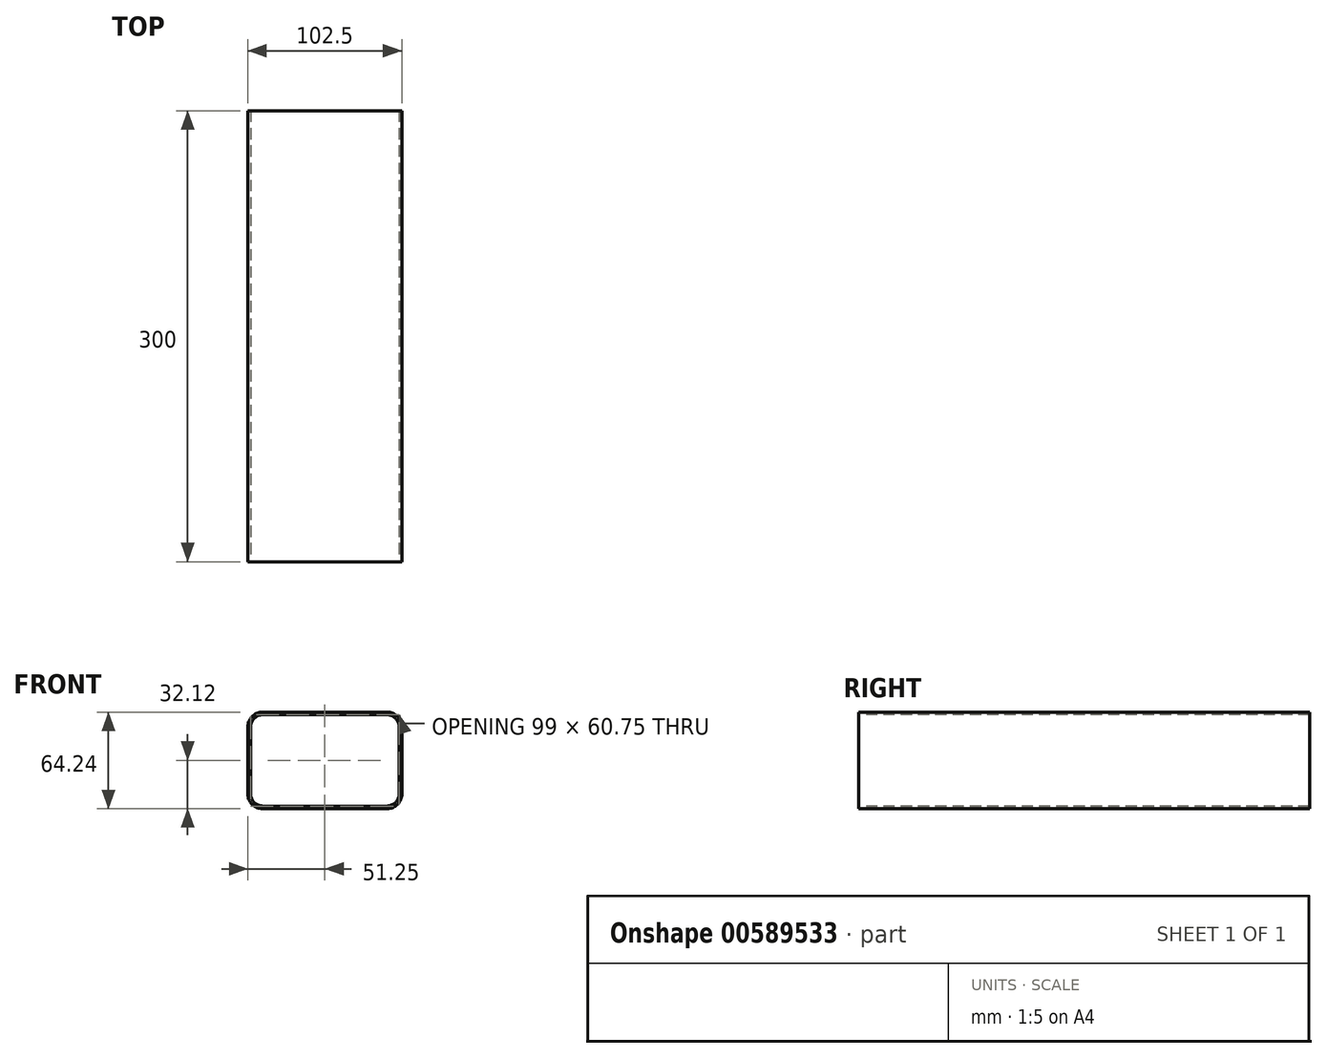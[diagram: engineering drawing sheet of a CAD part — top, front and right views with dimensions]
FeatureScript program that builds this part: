
annotation { "Feature Type Name" : "Feature", "Feature Type Description" : "" }
export const myFeature = defineFeature(function(context is Context, id is Id, definition is map)
    precondition{}
    {
        {
            var Q0;
            Q0=qCreatedBy(makeId("Front.planeOp"),FACE);
            var sketch = newSketch(context, id + "F0", { "sketchPlane" : qUnion([Q0]), "disableImprinting" : false});
            skLineSegment(sketch, "E0.bottom", {"start": v(41.25, 32.12) * mm, "end": v(-41.25, 32.12) * mm});
            skLineSegment(sketch, "E0.top", {"start": v(41.25, -32.13) * mm, "end": v(-41.25, -32.13) * mm});
            skLineSegment(sketch, "E0.left", {"start": v(51.25, 22.13) * mm, "end": v(51.25, -22.13) * mm});
            skLineSegment(sketch, "E0.right", {"start": v(-51.25, 22.12) * mm, "end": v(-51.25, -22.13) * mm});
            skPoint(sketch, "E0.middle", {"position": v(0, 0) * mm});
            skPoint(sketch, "E1.visualSharp", {"position": v(-51.25, 32.12) * mm});
            skArc(sketch, "E1.filletArc", {"start": v(-41.25, 32.12) * mm, "mid": v(-48.32, 29.2) * mm, "end": v(-51.25, 22.12) * mm});
            skPoint(sketch, "E2.visualSharp", {"position": v(51.25, 32.12) * mm});
            skArc(sketch, "E2.filletArc", {"start": v(51.25, 22.13) * mm, "mid": v(48.32, 29.2) * mm, "end": v(41.25, 32.13) * mm});
            skPoint(sketch, "E3.visualSharp", {"position": v(51.25, -32.13) * mm});
            skArc(sketch, "E3.filletArc", {"start": v(41.25, -32.13) * mm, "mid": v(48.32, -29.2) * mm, "end": v(51.25, -22.13) * mm});
            skPoint(sketch, "E4.visualSharp", {"position": v(-51.25, -32.13) * mm});
            skArc(sketch, "E4.filletArc", {"start": v(-51.25, -22.13) * mm, "mid": v(-48.32, -29.2) * mm, "end": v(-41.25, -32.13) * mm});
            skLineSegment(sketch, "E5.0", {"start": v(-49.5, 22.13) * mm, "end": v(-49.5, -22.13) * mm});
            skArc(sketch, "E5.1", {"start": v(-41.25, 30.38) * mm, "mid": v(-47.08, 27.96) * mm, "end": v(-49.5, 22.13) * mm});
            skArc(sketch, "E5.2", {"start": v(-49.5, -22.13) * mm, "mid": v(-47.08, -27.96) * mm, "end": v(-41.25, -30.38) * mm});
            skLineSegment(sketch, "E5.3", {"start": v(41.25, 30.38) * mm, "end": v(-41.25, 30.38) * mm});
            skLineSegment(sketch, "E5.4", {"start": v(41.25, -30.38) * mm, "end": v(-41.25, -30.38) * mm});
            skArc(sketch, "E5.5", {"start": v(41.25, -30.38) * mm, "mid": v(47.08, -27.96) * mm, "end": v(49.5, -22.13) * mm});
            skLineSegment(sketch, "E5.6", {"start": v(49.5, 22.13) * mm, "end": v(49.5, -22.13) * mm});
            skArc(sketch, "E5.7", {"start": v(49.5, 22.13) * mm, "mid": v(47.08, 27.96) * mm, "end": v(41.25, 30.38) * mm});
            skSolve(sketch);
        }
        {
            var Q0;
            Q0 = qSketchRegion(id + "F0", true);
            extrude(context, id + "F1", {"entities" : qUnion([Q0]), "flatOperationType" : FlatOperationType.REMOVE, "oppositeDirection" : true, "depth" : 300 * mm, "offsetDistance" : 25 * mm, "startOffsetBound" : StartOffsetType.BLIND, "startOffsetDistance" : 25 * mm, "domain" : OperationDomain.MODEL});
        }
    });
